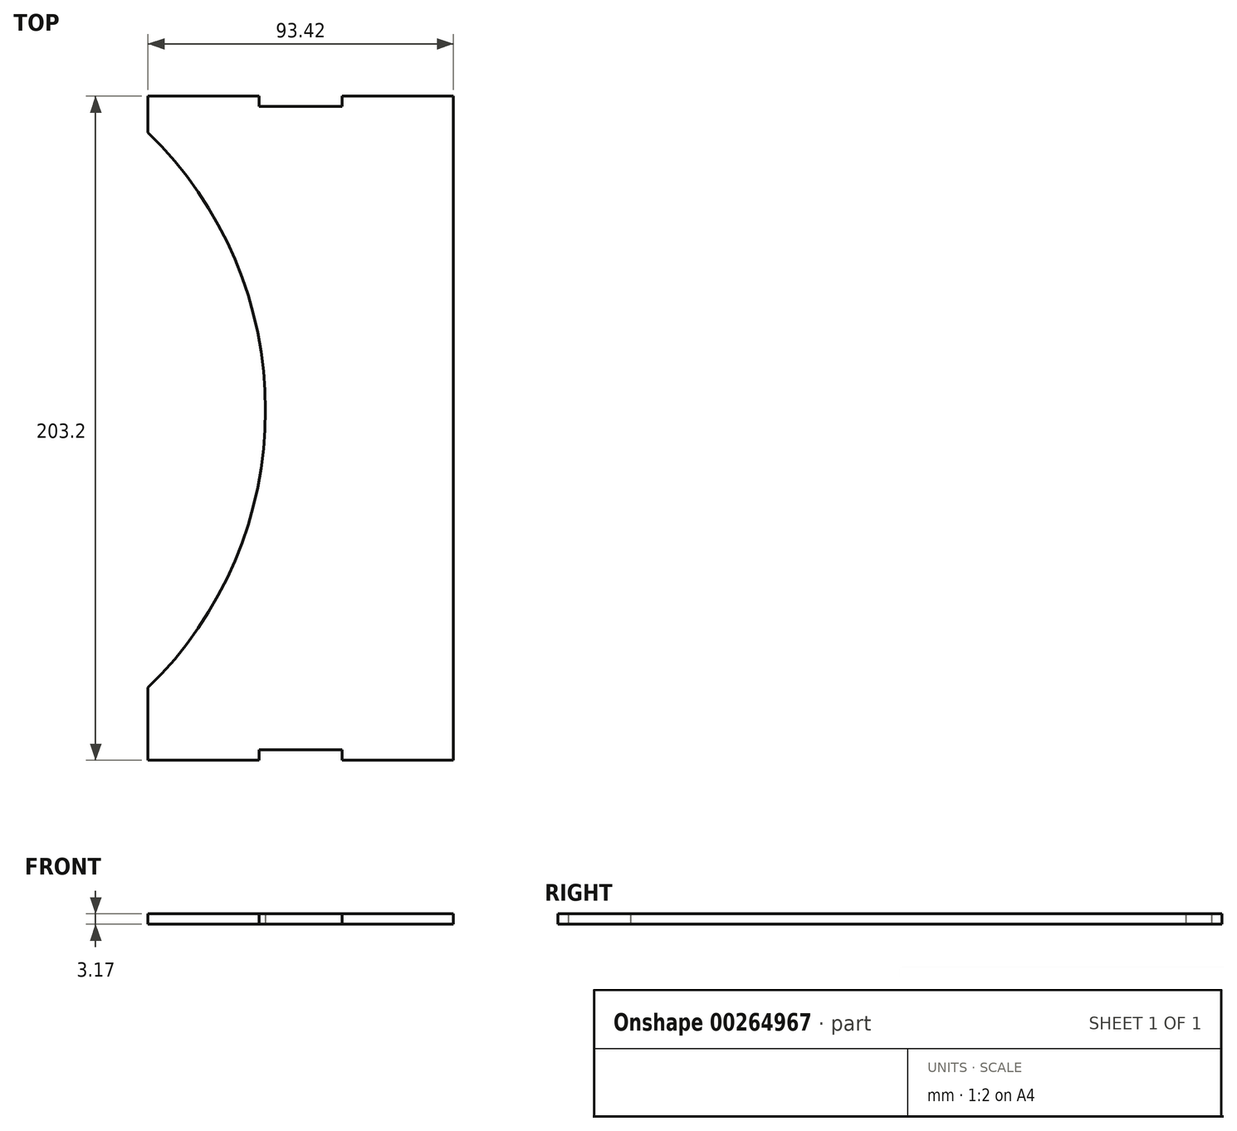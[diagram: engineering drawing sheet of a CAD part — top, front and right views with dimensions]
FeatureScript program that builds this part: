
annotation { "Feature Type Name" : "Feature", "Feature Type Description" : "" }
export const myFeature = defineFeature(function(context is Context, id is Id, definition is map)
    precondition{}
    {
        {
            var Q0;
            Q0=qCreatedBy(makeId("Top.planeOp"),FACE);
            var sketch = newSketch(context, id + "F0", { "sketchPlane" : qUnion([Q0])});
            skLineSegment(sketch, "E0", {"start": v(-42.07, -101.6) * mm, "end": v(-42.07, -79.38) * mm});
            skLineSegment(sketch, "E1", {"start": v(-42.07, -101.6) * mm, "end": v(-14.02, -101.6) * mm});
            skLineSegment(sketch, "E2.trimOffspring", {"start": v(17.34, -101.6) * mm, "end": v(51.35, -101.6) * mm});
            skLineSegment(sketch, "E3.MirrorCS", {"start": v(-42.07, 101.6) * mm, "end": v(-14.02, 101.6) * mm});
            skLineSegment(sketch, "E4.MirrorCS", {"start": v(24.58, 101.6) * mm, "end": v(51.35, 101.6) * mm});
            skPoint(sketch, "E5.endSnap0", {"position": v(38.6, 101.6) * mm});
            skLineSegment(sketch, "E6", {"start": v(50.34, -101.6) * mm, "end": v(51.35, -101.6) * mm});
            skLineSegment(sketch, "E7", {"start": v(51.35, -101.6) * mm, "end": v(51.35, 101.6) * mm});
            skPoint(sketch, "E5.end.orphan", {"position": v(49.45, 101.6) * mm});
            skLineSegment(sketch, "E8", {"start": v(-14.02, 101.6) * mm, "end": v(-13.77, 101.6) * mm});
            skLineSegment(sketch, "E9", {"start": v(-14.02, -101.6) * mm, "end": v(-13.77, -101.6) * mm});
            skLineSegment(sketch, "E10", {"start": v(-42.07, 101.6) * mm, "end": v(-42.07, 90.49) * mm});
            skPoint(sketch, "E11", {"position": v(-41.81, 5.52) * mm});
            skArc(sketch, "E12", {"start": v(-42.07, -79.38) * mm, "mid": v(-6.13, 5.56) * mm, "end": v(-42.07, 90.49) * mm});
            skLineSegment(sketch, "E13", {"start": v(-13.77, -101.6) * mm, "end": v(-8.06, -101.6) * mm});
            skLineSegment(sketch, "E14", {"start": v(-13.77, 101.6) * mm, "end": v(-8.06, 101.6) * mm});
            skPoint(sketch, "E15.orphan", {"position": v(-42.07, 104.78) * mm});
            skLineSegment(sketch, "E16", {"start": v(17.34, 101.6) * mm, "end": v(24.58, 101.6) * mm});
            skLineSegment(sketch, "E17", {"start": v(-42.07, -101.6) * mm, "end": v(-8.06, -101.6) * mm});
            skLineSegment(sketch, "E18.MirrorCS", {"start": v(-8.06, -98.43) * mm, "end": v(-8.06, -101.6) * mm});
            skLineSegment(sketch, "E19.MirrorCS", {"start": v(4.64, -98.43) * mm, "end": v(-8.06, -98.43) * mm});
            skLineSegment(sketch, "E20.MirrorCS", {"start": v(4.64, -98.43) * mm, "end": v(17.34, -98.43) * mm});
            skLineSegment(sketch, "E21.MirrorCS", {"start": v(17.34, -98.43) * mm, "end": v(17.34, -101.6) * mm});
            skLineSegment(sketch, "E22.MirrorCS", {"start": v(4.64, 98.43) * mm, "end": v(-8.06, 98.43) * mm});
            skLineSegment(sketch, "E23.MirrorCS", {"start": v(-8.06, 98.43) * mm, "end": v(-8.06, 101.6) * mm});
            skLineSegment(sketch, "E24.MirrorCS", {"start": v(4.64, 98.43) * mm, "end": v(17.34, 98.43) * mm});
            skLineSegment(sketch, "E25", {"start": v(17.34, 101.6) * mm, "end": v(17.34, 98.43) * mm});
            skSolve(sketch);
        }
        {
            var Q0;
            Q0=makeQuery(id+"F0.imprint","IMPRINT",FACE,{"disambiguationData":[TD([[makeQuery(id+"F0.imprint","IMPRINT",EDGE,{"derivedFrom":sQuery(id+"F0.wireOp",EDGE,"E0")}),-1.0]])]});
            extrude(context, id + "F1", {"entities" : qUnion([Q0]), "depth" : 3.17 * mm});
        }
    });
